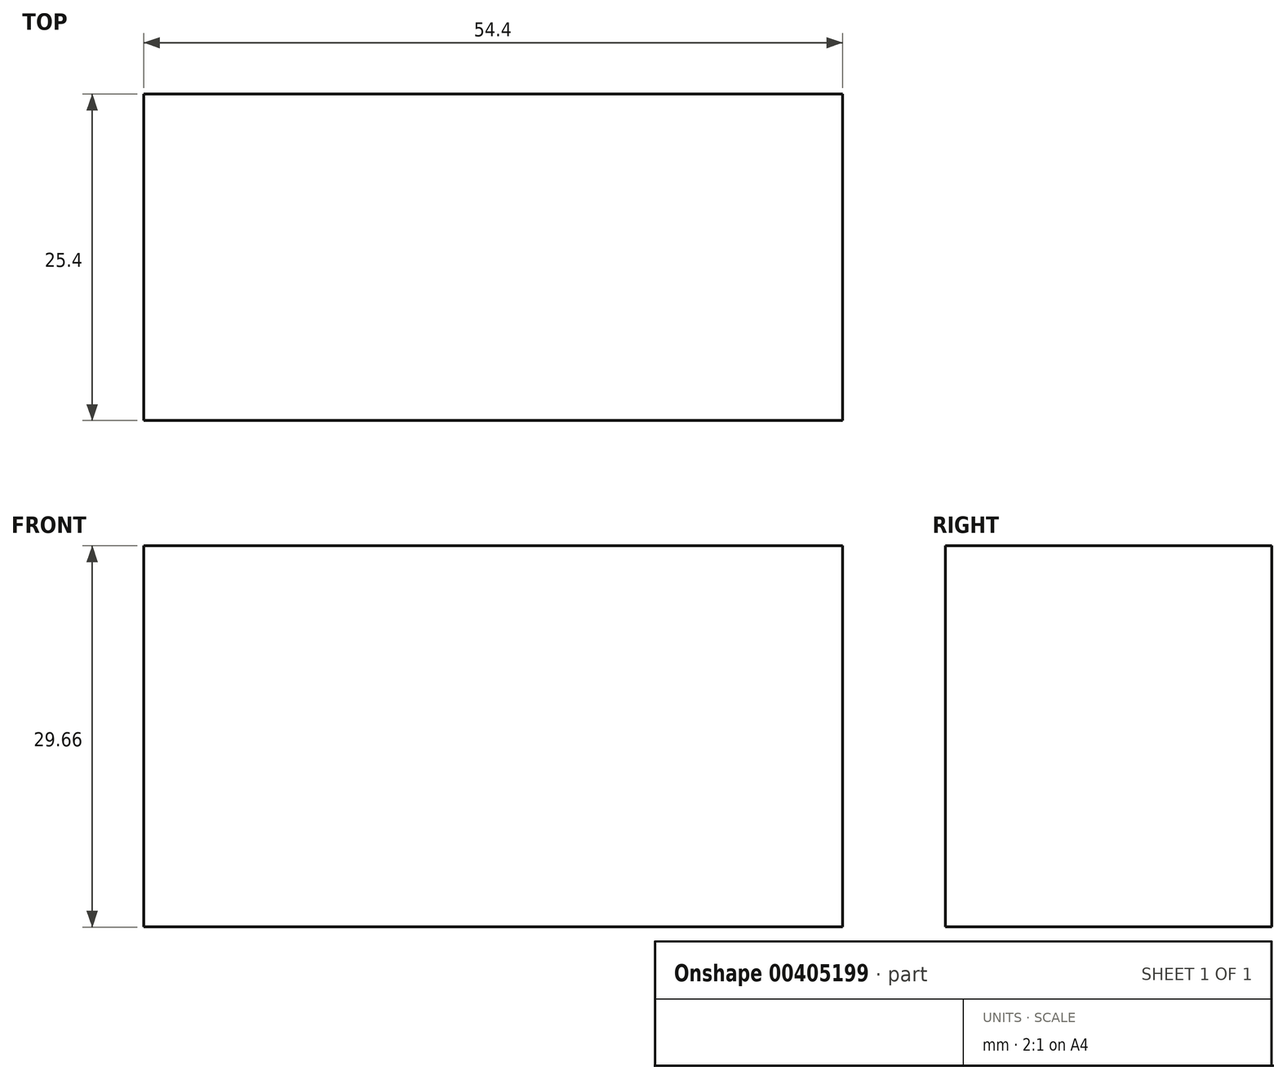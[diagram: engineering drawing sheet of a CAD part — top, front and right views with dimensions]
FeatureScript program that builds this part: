
annotation { "Feature Type Name" : "Feature", "Feature Type Description" : "" }
export const myFeature = defineFeature(function(context is Context, id is Id, definition is map)
    precondition{}
    {
        {
            var Q0;
            Q0=qCreatedBy(makeId("Front.planeOp"),FACE);
            var sketch = newSketch(context, id + "F0", { "sketchPlane" : qUnion([Q0])});
            skLineSegment(sketch, "E0.bottom", {"start": v(0, 0) * mm, "end": v(54.4, 0) * mm});
            skLineSegment(sketch, "E0.top", {"start": v(0, -29.66) * mm, "end": v(54.4, -29.66) * mm});
            skLineSegment(sketch, "E0.left", {"start": v(0, 0) * mm, "end": v(0, -29.66) * mm});
            skLineSegment(sketch, "E0.right", {"start": v(54.4, 0) * mm, "end": v(54.4, -29.66) * mm});
            skSolve(sketch);
        }
        {
            var Q0;
            Q0=makeQuery(id+"F0.imprint","IMPRINT",FACE,{"disambiguationData":[TD([[makeQuery(id+"F0.imprint","IMPRINT",EDGE,{"derivedFrom":sQuery(id+"F0.wireOp",EDGE,"E0.bottom")}),-1.0]])]});
            extrude(context, id + "F1", {"entities" : qUnion([Q0]), "depth" : 25.4 * mm});
        }
    });
